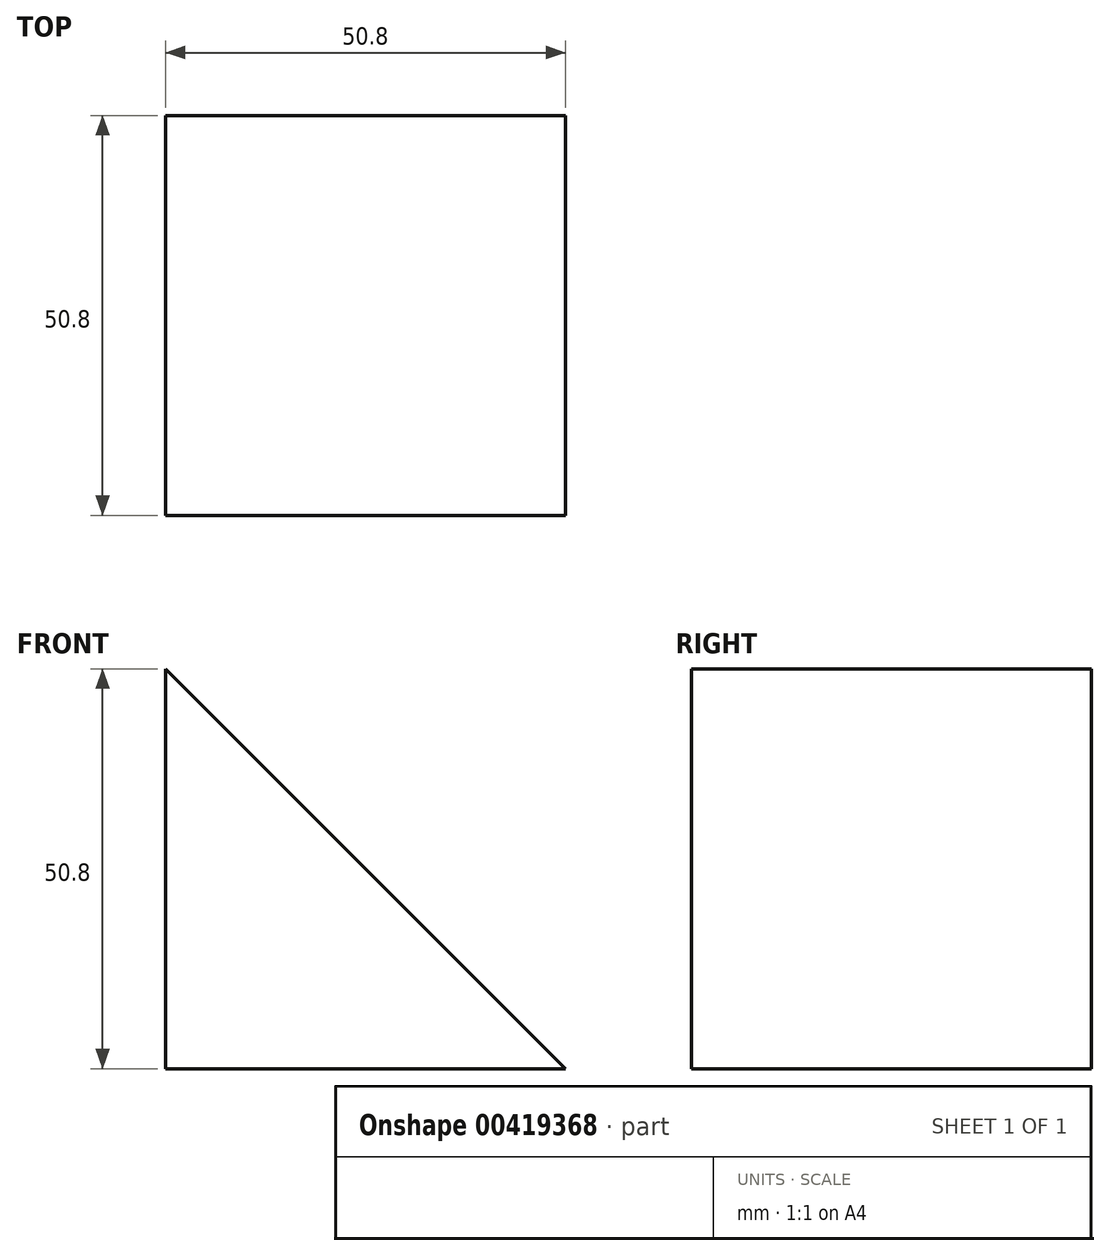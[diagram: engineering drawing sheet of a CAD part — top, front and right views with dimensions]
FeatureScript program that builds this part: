
annotation { "Feature Type Name" : "Feature", "Feature Type Description" : "" }
export const myFeature = defineFeature(function(context is Context, id is Id, definition is map)
    precondition{}
    {
        {
            var Q0;
            Q0=qCreatedBy(makeId("Front.planeOp"),FACE);
            var sketch = newSketch(context, id + "F0", { "sketchPlane" : qUnion([Q0])});
            skLineSegment(sketch, "E0", {"start": v(-45.45, 66.46) * mm, "end": v(-45.45, 15.66) * mm});
            skLineSegment(sketch, "E1", {"start": v(-45.45, 15.66) * mm, "end": v(5.35, 15.66) * mm});
            skLineSegment(sketch, "E2", {"start": v(5.35, 15.66) * mm, "end": v(-45.45, 66.46) * mm});
            skSolve(sketch);
        }
        {
            var Q0;
            Q0 = qSketchRegion(id + "F0", true);
            extrude(context, id + "F1", {"entities" : qUnion([Q0]), "depth" : 50.8 * mm});
        }
    });
